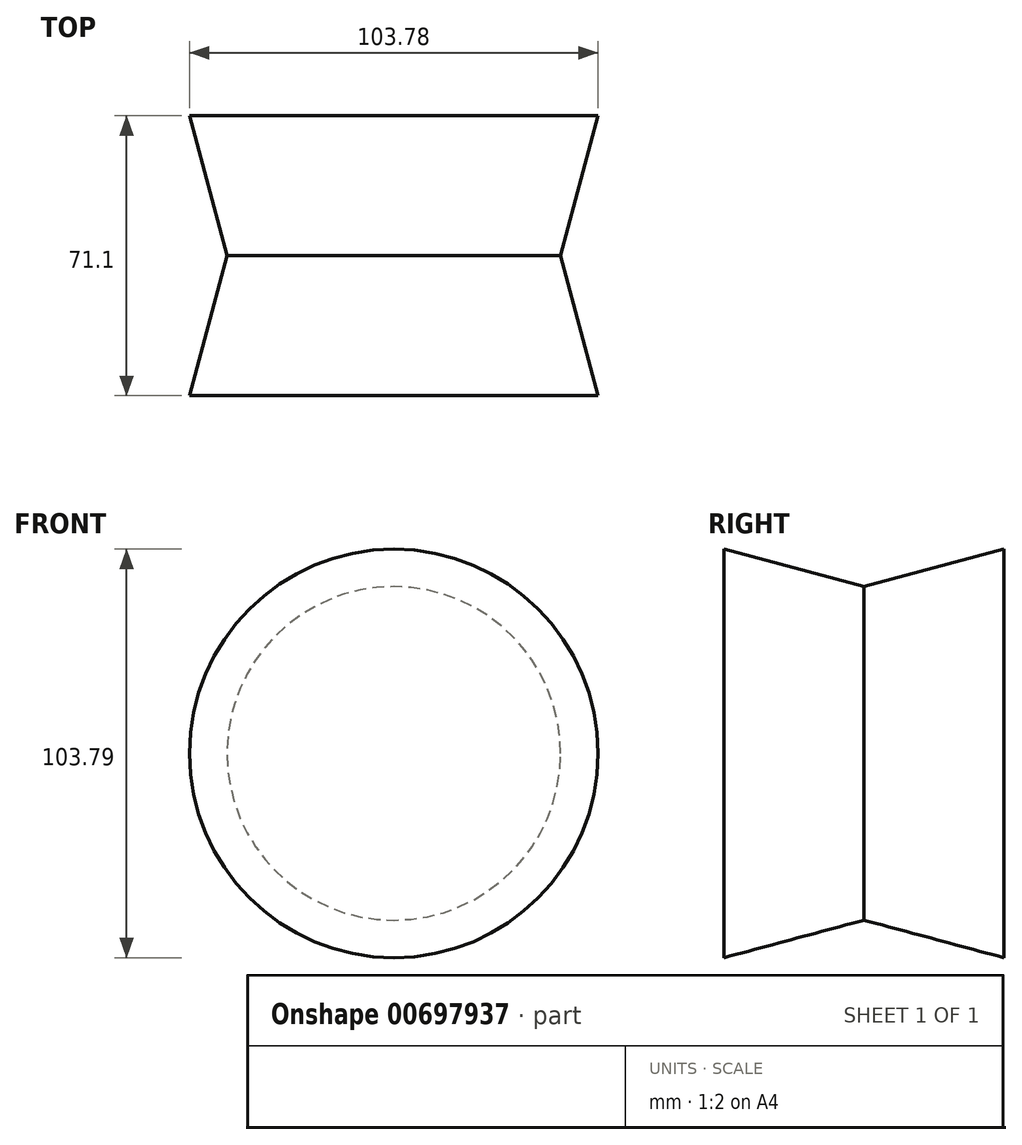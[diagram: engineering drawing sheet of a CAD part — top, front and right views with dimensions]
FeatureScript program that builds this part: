
annotation { "Feature Type Name" : "Feature", "Feature Type Description" : "" }
export const myFeature = defineFeature(function(context is Context, id is Id, definition is map)
    precondition{}
    {
        {
            var Q0;
            Q0=qCreatedBy(makeId("Front.planeOp"),FACE);
            var sketch = newSketch(context, id + "F0", { "sketchPlane" : qUnion([Q0])});
            skCircle(sketch, "E0", {"center": v(-42.1, -4.75) * mm, "radius": 42.37 * mm});
            skPoint(sketch, "E0.first.point", {"position": v(-37.12, 37.33) * mm});
            skPoint(sketch, "E0.second.point", {"position": v(0.23, -3.05) * mm});
            skPoint(sketch, "E0.third.point", {"position": v(0, 0) * mm});
            skSolve(sketch);
        }
        {
            var Q0;
            Q0=makeQuery(id+"F0.imprint","IMPRINT",FACE,{"disambiguationData":[TD([[makeQuery(id+"F0.imprint","IMPRINT",EDGE,{"derivedFrom":sQuery(id+"F0.wireOp",EDGE,"E0")}),1.0]])]});
            extrude(context, id + "F1", {"entities" : qUnion([Q0]), "endBound" : BoundingType.SYMMETRIC, "depth" : 71.1 * mm, "offsetDistance" : 25 * mm, "hasDraft" : true, "draftAngle" : 15 * degree, "hasSecondDirection" : true, "secondDirectionOppositeDirection" : true, "secondDirectionDepth" : 25 * mm});
        }
    });
